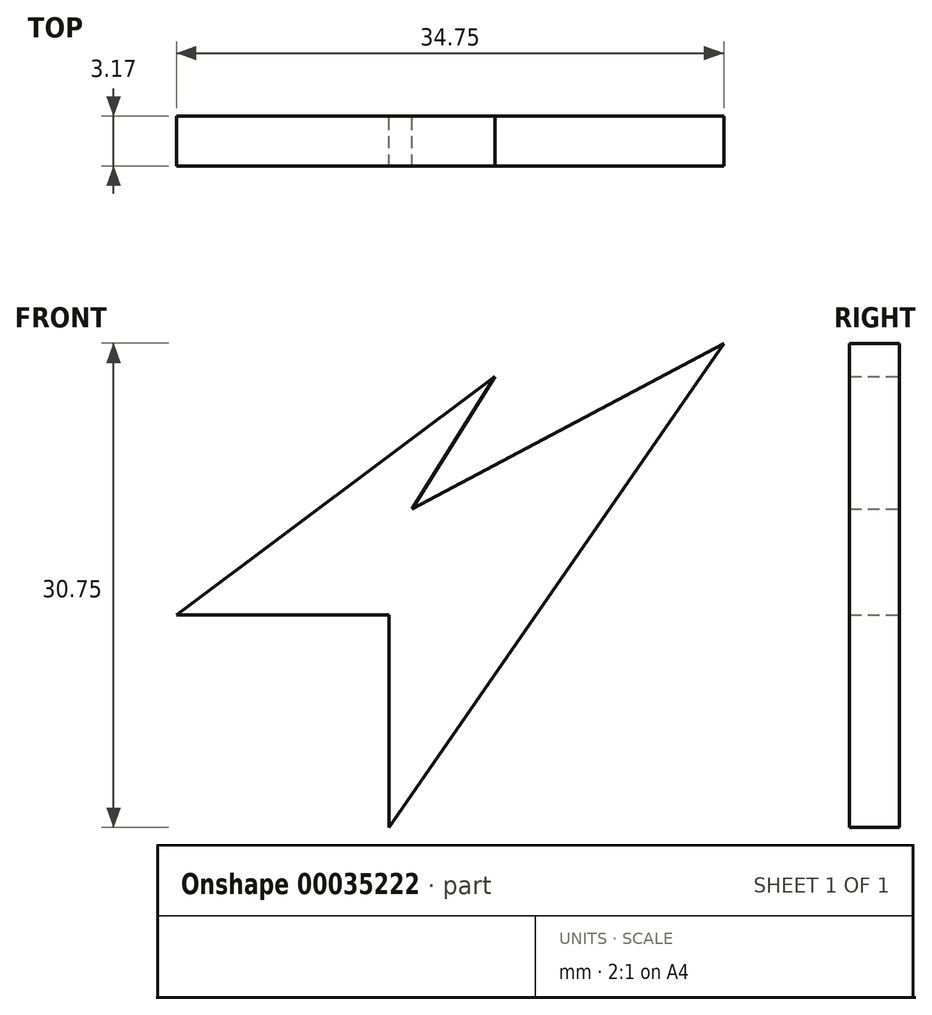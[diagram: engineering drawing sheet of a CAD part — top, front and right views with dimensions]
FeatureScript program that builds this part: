
annotation { "Feature Type Name" : "Feature", "Feature Type Description" : "" }
export const myFeature = defineFeature(function(context is Context, id is Id, definition is map)
    precondition{}
    {
        {
            var Q0;
            Q0=qCreatedBy(makeId("Front.planeOp"),FACE);
            var sketch = newSketch(context, id + "F0", { "sketchPlane" : qUnion([Q0])});
            skLineSegment(sketch, "E0", {"start": v(8.63, 35.49) * mm, "end": v(22.11, 35.49) * mm});
            skLineSegment(sketch, "E1", {"start": v(22.11, 35.49) * mm, "end": v(22.11, 22) * mm});
            skLineSegment(sketch, "E2", {"start": v(22.11, 22) * mm, "end": v(43.38, 52.76) * mm});
            skLineSegment(sketch, "E3", {"start": v(43.38, 52.76) * mm, "end": v(23.59, 42.23) * mm});
            skLineSegment(sketch, "E4", {"start": v(23.59, 42.23) * mm, "end": v(28.85, 50.65) * mm});
            skLineSegment(sketch, "E5", {"start": v(28.85, 50.65) * mm, "end": v(8.63, 35.49) * mm});
            skSolve(sketch);
        }
        {
            var Q0;
            Q0=makeQuery(id+"F0.imprint","IMPRINT",FACE,{"disambiguationData":[TD([[makeQuery(id+"F0.imprint","IMPRINT",EDGE,{"derivedFrom":sQuery(id+"F0.wireOp",EDGE,"E0")}),1.0]])]});
            extrude(context, id + "F1", {"entities" : qUnion([Q0]), "depth" : 3.17 * mm});
        }
    });
